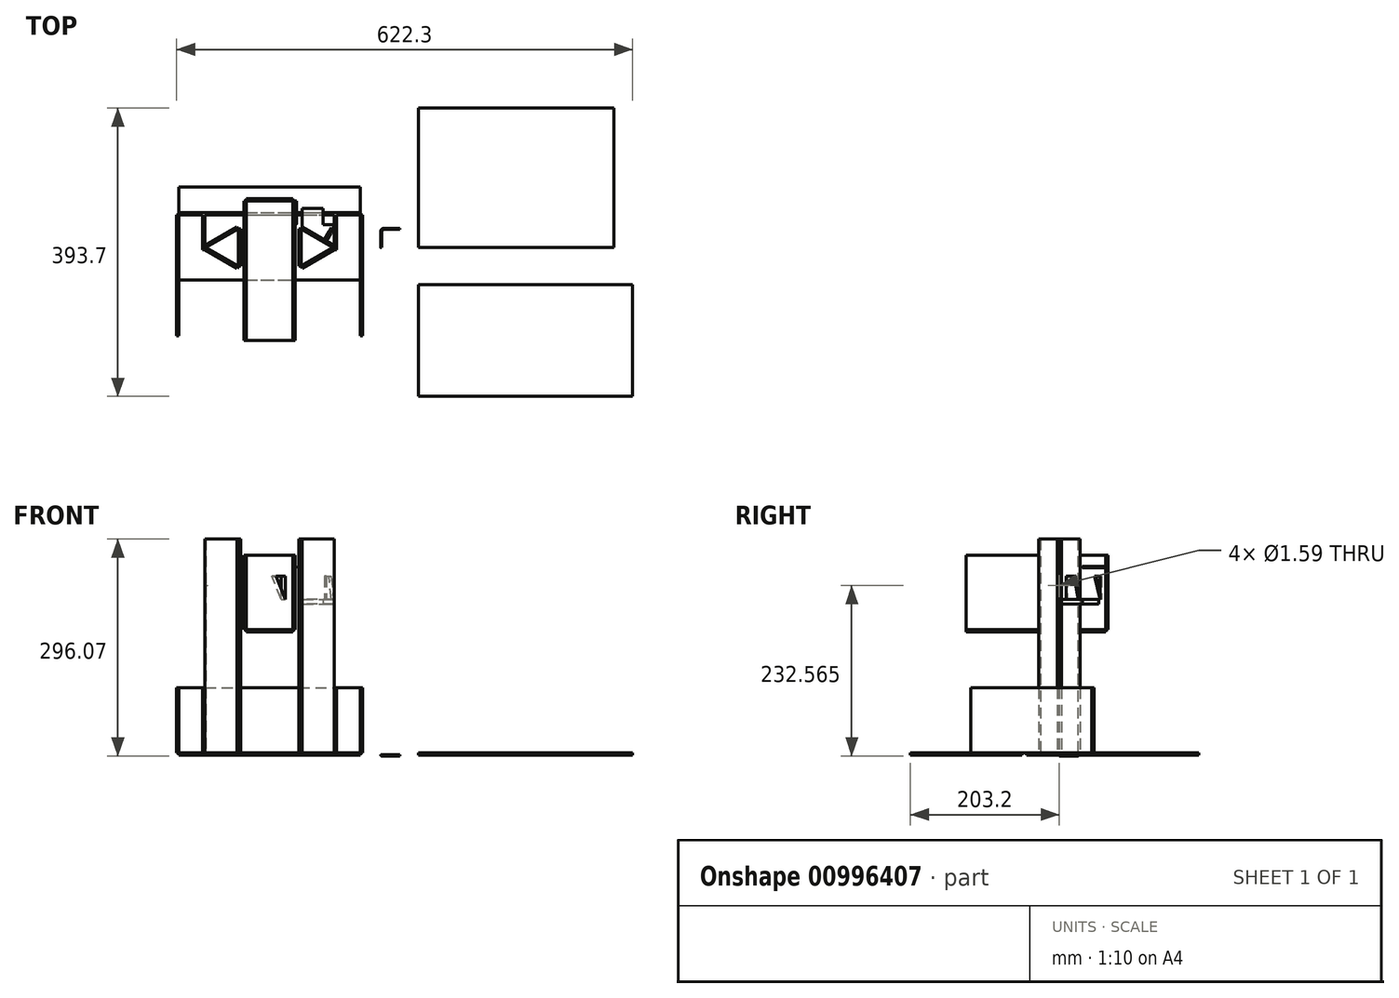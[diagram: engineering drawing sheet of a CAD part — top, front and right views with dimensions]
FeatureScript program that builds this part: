
annotation { "Feature Type Name" : "Feature", "Feature Type Description" : "" }
export const myFeature = defineFeature(function(context is Context, id is Id, definition is map)
    precondition{}
    {
        {
            var Q0;
            Q0=qCreatedBy(makeId("Top.planeOp"),FACE);
            var sketch = newSketch(context, id + "F0", { "sketchPlane" : qUnion([Q0])});
            skLineSegment(sketch, "E0.bottom", {"start": v(-123.83, -44.45) * mm, "end": v(123.83, -44.45) * mm});
            skLineSegment(sketch, "E0.top", {"start": v(-123.83, 44.45) * mm, "end": v(123.83, 44.45) * mm});
            skLineSegment(sketch, "E0.left", {"start": v(-123.83, -44.45) * mm, "end": v(-123.83, 44.45) * mm});
            skLineSegment(sketch, "E0.right", {"start": v(123.83, -44.45) * mm, "end": v(123.83, 44.45) * mm});
            skPoint(sketch, "E0.middle", {"position": v(0, 0) * mm});
            skSolve(sketch);
        }
        {
            var Q0;
            Q0 = qSketchRegion(id + "F0", true);
            extrude(context, id + "F1", {"entities" : qUnion([Q0]), "depth" : 3.17 * mm, "offsetDistance" : 25.4 * mm});
        }
        {
            var Q0;
            Q0=makeQuery(id+"F1.opExtrude","CAP_FACE",FACE,{"disambiguationData":[OSD([sQuery(id+"F0.wireOp",EDGE,"E0.bottom"),sQuery(id+"F0.wireOp",EDGE,"E0.top"),sQuery(id+"F0.wireOp",EDGE,"E0.left"),sQuery(id+"F0.wireOp",EDGE,"E0.right")])],"isStart":false});
            var sketch = newSketch(context, id + "F2", { "sketchPlane" : qUnion([Q0])});
            skLineSegment(sketch, "E1.bottom", {"start": v(-123.83, 44.45) * mm, "end": v(-127, 44.45) * mm});
            skLineSegment(sketch, "E1.top", {"start": v(-123.82, -120.65) * mm, "end": v(-127, -120.65) * mm});
            skLineSegment(sketch, "E1.left", {"start": v(-123.83, 44.45) * mm, "end": v(-123.82, -120.65) * mm});
            skLineSegment(sketch, "E1.right", {"start": v(-127, 44.45) * mm, "end": v(-127, -120.65) * mm});
            skSolve(sketch);
        }
        {
            var Q0;
            Q0 = qSketchRegion(id + "F2", true);
            extrude(context, id + "F3", {"entities" : qUnion([Q0]), "depth" : 88.9 * mm, "offsetDistance" : 25.4 * mm});
        }
        {
            var Q0;
            Q0=makeQuery(id+"F3.opExtrude","SWEPT_BODY",BODY,{"disambiguationData":[OSD([sQuery(id+"F2.wireOp",EDGE,"E1.bottom"),sQuery(id+"F2.wireOp",EDGE,"E1.top"),sQuery(id+"F2.wireOp",EDGE,"E1.left"),sQuery(id+"F2.wireOp",EDGE,"E1.right")])]});
            var Q1;
            Q1=qCreatedBy(makeId("Right.planeOp"),FACE);
            mirror(context, id + "F4", {"operationType" : NewBodyOperationType.ADD, "entities" : qUnion([Q0]), "mirrorPlane" : qUnion([Q1])});
        }
        {
            var Q0;
            Q0=makeQuery(id+"F1.opExtrude","CAP_FACE",FACE,{"disambiguationData":[OSD([sQuery(id+"F0.wireOp",EDGE,"E0.bottom"),sQuery(id+"F0.wireOp",EDGE,"E0.top"),sQuery(id+"F0.wireOp",EDGE,"E0.left"),sQuery(id+"F0.wireOp",EDGE,"E0.right")])],"isStart":false});
            var sketch = newSketch(context, id + "F5", { "sketchPlane" : qUnion([Q0])});
            skLineSegment(sketch, "E2.bottom", {"start": v(-123.83, 44.45) * mm, "end": v(123.83, 44.45) * mm});
            skLineSegment(sketch, "E2.top", {"start": v(-123.83, 47.62) * mm, "end": v(123.83, 47.62) * mm});
            skLineSegment(sketch, "E2.left", {"start": v(-123.83, 44.45) * mm, "end": v(-123.83, 47.62) * mm});
            skLineSegment(sketch, "E2.right", {"start": v(123.83, 44.45) * mm, "end": v(123.83, 47.62) * mm});
            skSolve(sketch);
        }
        {
            var Q0;
            Q0 = qSketchRegion(id + "F5", true);
            var Q1;
            Q1=makeQuery(id+"F3.opExtrude","CAP_FACE",FACE,{"disambiguationData":[OSD([sQuery(id+"F2.wireOp",EDGE,"E1.bottom"),sQuery(id+"F2.wireOp",EDGE,"E1.top"),sQuery(id+"F2.wireOp",EDGE,"E1.left"),sQuery(id+"F2.wireOp",EDGE,"E1.right")])],"isStart":false});
            extrude(context, id + "F6", {"entities" : qUnion([Q0]), "endBound" : BoundingType.UP_TO_SURFACE, "depth" : 25.4 * mm, "endBoundEntityFace" : qUnion([Q1]), "offsetDistance" : 25.4 * mm});
        }
        {
            var Q0;
            Q0=makeQuery(id+"F1.opExtrude","CAP_FACE",FACE,{"disambiguationData":[OSD([sQuery(id+"F0.wireOp",EDGE,"E0.bottom"),sQuery(id+"F0.wireOp",EDGE,"E0.top"),sQuery(id+"F0.wireOp",EDGE,"E0.left"),sQuery(id+"F0.wireOp",EDGE,"E0.right")])],"isStart":false});
            var sketch = newSketch(context, id + "F7", { "sketchPlane" : qUnion([Q0])});
            skLineSegment(sketch, "E3", {"start": v(0, 0) * mm, "end": v(39.69, 0) * mm, "construction": true});
            skLineSegment(sketch, "E4", {"start": v(0, 0) * mm, "end": v(-39.69, 0) * mm, "construction": true});
            skLineSegment(sketch, "E5", {"start": v(-39.69, 25.4) * mm, "end": v(-39.69, -25.4) * mm, "construction": true});
            skLineSegment(sketch, "E6.bottom", {"start": v(-39.69, 25.4) * mm, "end": v(-42.86, 25.4) * mm});
            skLineSegment(sketch, "E6.top", {"start": v(-39.69, -25.4) * mm, "end": v(-42.86, -25.4) * mm});
            skLineSegment(sketch, "E6.left", {"start": v(-39.69, 25.4) * mm, "end": v(-39.69, -25.4) * mm});
            skLineSegment(sketch, "E6.right", {"start": v(-42.86, 25.4) * mm, "end": v(-42.86, -25.4) * mm});
            skSolve(sketch);
        }
        {
            var Q0;
            Q0 = qSketchRegion(id + "F7", true);
            extrude(context, id + "F8", {"entities" : qUnion([Q0]), "depth" : 292.1 * mm, "offsetDistance" : 25.4 * mm});
        }
        {
            var Q0;
            Q0=makeQuery(id+"F1.opExtrude","CAP_FACE",FACE,{"disambiguationData":[OSD([sQuery(id+"F0.wireOp",EDGE,"E0.bottom"),sQuery(id+"F0.wireOp",EDGE,"E0.top"),sQuery(id+"F0.wireOp",EDGE,"E0.left"),sQuery(id+"F0.wireOp",EDGE,"E0.right")])],"isStart":false});
            var sketch = newSketch(context, id + "F9", { "sketchPlane" : qUnion([Q0])});
            skLineSegment(sketch, "E7", {"start": v(-42.86, 25.4) * mm, "end": v(-86.86, 0) * mm, "construction": true});
            skLineSegment(sketch, "E8", {"start": v(-86.86, 0) * mm, "end": v(-42.86, -25.4) * mm, "construction": true});
            skLineSegment(sketch, "E9.bottom", {"start": v(-88.44, 2.75) * mm, "end": v(-44.45, 28.15) * mm});
            skLineSegment(sketch, "E9.top", {"start": v(-86.86, 0) * mm, "end": v(-42.86, 25.4) * mm});
            skLineSegment(sketch, "E9.left", {"start": v(-88.44, 2.75) * mm, "end": v(-86.86, 0) * mm});
            skLineSegment(sketch, "E9.right", {"start": v(-44.45, 28.15) * mm, "end": v(-42.86, 25.4) * mm});
            skLineSegment(sketch, "E10.bottom", {"start": v(-86.86, 0) * mm, "end": v(-42.86, -25.4) * mm});
            skLineSegment(sketch, "E10.top", {"start": v(-88.44, -2.75) * mm, "end": v(-44.45, -28.15) * mm});
            skLineSegment(sketch, "E10.left", {"start": v(-86.86, 0) * mm, "end": v(-88.44, -2.75) * mm});
            skLineSegment(sketch, "E10.right", {"start": v(-42.86, -25.4) * mm, "end": v(-44.45, -28.15) * mm});
            skSolve(sketch);
        }
        {
            var Q0;
            Q0=makeQuery(id+"F9.imprint","IMPRINT",FACE,{"disambiguationData":[TD([[makeQuery(id+"F9.imprint","IMPRINT",EDGE,{"derivedFrom":sQuery(id+"F9.wireOp",EDGE,"E10.bottom")}),-1.0]])]});
            var Q1;
            Q1=makeQuery(id+"F9.imprint","IMPRINT",FACE,{"disambiguationData":[TD([[makeQuery(id+"F9.imprint","IMPRINT",EDGE,{"derivedFrom":sQuery(id+"F9.wireOp",EDGE,"E9.bottom")}),-1.0]])]});
            var Q2;
            Q2=makeQuery(id+"F8.opExtrude","CAP_FACE",FACE,{"disambiguationData":[OSD([sQuery(id+"F7.wireOp",EDGE,"E6.bottom"),sQuery(id+"F7.wireOp",EDGE,"E6.top"),sQuery(id+"F7.wireOp",EDGE,"E6.left"),sQuery(id+"F7.wireOp",EDGE,"E6.right")])],"isStart":false});
            extrude(context, id + "F10", {"entities" : qUnion([Q0, Q1]), "endBound" : BoundingType.UP_TO_SURFACE, "depth" : 25.4 * mm, "endBoundEntityFace" : qUnion([Q2]), "offsetDistance" : 25.4 * mm});
        }
        {
            var Q0;
            Q0=makeQuery(id+"F10.opExtrude","SWEPT_BODY",BODY,{"disambiguationData":[OSD([sQuery(id+"F9.wireOp",EDGE,"E10.bottom"),sQuery(id+"F9.wireOp",EDGE,"E10.top"),sQuery(id+"F9.wireOp",EDGE,"E10.left"),sQuery(id+"F9.wireOp",EDGE,"E10.right")])]});
            var Q1;
            Q1=makeQuery(id+"F10.opExtrude","SWEPT_BODY",BODY,{"disambiguationData":[OSD([sQuery(id+"F9.wireOp",EDGE,"E9.bottom"),sQuery(id+"F9.wireOp",EDGE,"E9.top"),sQuery(id+"F9.wireOp",EDGE,"E9.left"),sQuery(id+"F9.wireOp",EDGE,"E9.right")])]});
            var Q2;
            Q2=makeQuery(id+"F8.opExtrude","SWEPT_BODY",BODY,{"disambiguationData":[OSD([sQuery(id+"F7.wireOp",EDGE,"E6.bottom"),sQuery(id+"F7.wireOp",EDGE,"E6.top"),sQuery(id+"F7.wireOp",EDGE,"E6.left"),sQuery(id+"F7.wireOp",EDGE,"E6.right")])]});
            var Q3;
            Q3=qCreatedBy(makeId("Right.planeOp"),FACE);
            mirror(context, id + "F11", {"entities" : qUnion([Q0, Q1, Q2]), "mirrorPlane" : qUnion([Q3])});
        }
        {
            var Q0;
            Q0=makeQuery(id+"F1.opExtrude","CAP_FACE",FACE,{"disambiguationData":[OSD([sQuery(id+"F0.wireOp",EDGE,"E0.bottom"),sQuery(id+"F0.wireOp",EDGE,"E0.top"),sQuery(id+"F0.wireOp",EDGE,"E0.left"),sQuery(id+"F0.wireOp",EDGE,"E0.right")])],"isStart":false});
            var sketch = newSketch(context, id + "F12", { "sketchPlane" : qUnion([Q0])});
            skLineSegment(sketch, "E11.bottom", {"start": v(-91.62, 44.45) * mm, "end": v(-88.44, 44.45) * mm});
            skLineSegment(sketch, "E11.top", {"start": v(-91.62, -2.75) * mm, "end": v(-88.44, -2.75) * mm});
            skLineSegment(sketch, "E11.left", {"start": v(-91.62, 44.45) * mm, "end": v(-91.62, -2.75) * mm});
            skLineSegment(sketch, "E11.right", {"start": v(-88.44, 44.45) * mm, "end": v(-88.44, -2.75) * mm});
            skSolve(sketch);
        }
        {
            var Q0;
            Q0 = qSketchRegion(id + "F12", true);
            var Q1;
            Q1=makeQuery(id+"F6.opExtrude","CAP_FACE",FACE,{"disambiguationData":[OSD([sQuery(id+"F5.wireOp",EDGE,"E2.bottom"),sQuery(id+"F5.wireOp",EDGE,"E2.top"),sQuery(id+"F5.wireOp",EDGE,"E2.left"),sQuery(id+"F5.wireOp",EDGE,"E2.right")])],"isStart":false});
            extrude(context, id + "F13", {"entities" : qUnion([Q0]), "endBound" : BoundingType.UP_TO_SURFACE, "depth" : 101.6 * mm, "endBoundEntityFace" : qUnion([Q1]), "offsetDistance" : 25.4 * mm});
        }
        {
            var Q0;
            Q0=makeQuery(id+"F1.opExtrude","CAP_FACE",FACE,{"disambiguationData":[OSD([sQuery(id+"F0.wireOp",EDGE,"E0.bottom"),sQuery(id+"F0.wireOp",EDGE,"E0.top"),sQuery(id+"F0.wireOp",EDGE,"E0.left"),sQuery(id+"F0.wireOp",EDGE,"E0.right")])],"isStart":false});
            var sketch = newSketch(context, id + "F14", { "sketchPlane" : qUnion([Q0])});
            skLineSegment(sketch, "E12.bottom", {"start": v(88.44, -2.75) * mm, "end": v(91.62, -2.75) * mm});
            skLineSegment(sketch, "E12.top", {"start": v(88.44, 44.45) * mm, "end": v(91.62, 44.45) * mm});
            skLineSegment(sketch, "E12.left", {"start": v(88.44, 44.45) * mm, "end": v(88.44, -2.75) * mm});
            skLineSegment(sketch, "E12.right", {"start": v(91.62, 44.45) * mm, "end": v(91.62, -2.75) * mm});
            skSolve(sketch);
        }
        {
            var Q0;
            Q0 = qSketchRegion(id + "F14", true);
            var Q1;
            Q1=makeQuery(id+"F4.opPattern","COPY",FACE,{"derivedFrom":makeQuery(id+"F3.opExtrude","CAP_FACE",FACE,{"disambiguationData":[OSD([sQuery(id+"F2.wireOp",EDGE,"E1.bottom"),sQuery(id+"F2.wireOp",EDGE,"E1.top"),sQuery(id+"F2.wireOp",EDGE,"E1.left"),sQuery(id+"F2.wireOp",EDGE,"E1.right")])],"isStart":false}),"instanceName":"1"});
            extrude(context, id + "F15", {"entities" : qUnion([Q0]), "endBound" : BoundingType.UP_TO_SURFACE, "depth" : 25.4 * mm, "endBoundEntityFace" : qUnion([Q1]), "offsetDistance" : 25.4 * mm});
        }
        {
            var Q0;
            Q0=qCreatedBy(makeId("Right.planeOp"),FACE);
            var sketch = newSketch(context, id + "F16", { "sketchPlane" : qUnion([Q0])});
            skCircle(sketch, "E13", {"center": v(0, 231.78) * mm, "radius": 0.8 * mm});
            skLineSegment(sketch, "E14.0", {"start": v(25.4, 295.28) * mm, "end": v(-25.4, 295.28) * mm, "construction": true});
            skLineSegment(sketch, "E15", {"start": v(0, 295.28) * mm, "end": v(0, 231.78) * mm, "construction": true});
            skSolve(sketch);
        }
        {
            var Q0;
            Q0 = qSketchRegion(id + "F16", true);
            extrude(context, id + "F17", {"entities" : qUnion([Q0]), "operationType" : NewBodyOperationType.REMOVE, "endBound" : BoundingType.SYMMETRIC, "oppositeDirection" : true, "depth" : 101.6 * mm, "offsetDistance" : 25.4 * mm});
        }
        {
            var Q0;
            Q0=makeQuery(id+"F8.opExtrude","CAP_FACE",FACE,{"disambiguationData":[OSD([sQuery(id+"F7.wireOp",EDGE,"E6.bottom"),sQuery(id+"F7.wireOp",EDGE,"E6.top"),sQuery(id+"F7.wireOp",EDGE,"E6.left"),sQuery(id+"F7.wireOp",EDGE,"E6.right")])],"isStart":false});
            cPlane(context, id + "F18", {"entities" : qUnion([Q0]), "cplaneType" : CPlaneType.OFFSET, "offset" : 127 * mm, "oppositeDirection" : true, "width" : 152.4 * mm, "height" : 152.4 * mm});
        }
        {
            var Q0;
            Q0=qCreatedBy(id+"F18.planeOp",FACE);
            var sketch = newSketch(context, id + "F19", { "sketchPlane" : qUnion([Q0])});
            skLineSegment(sketch, "E16.bottom", {"start": v(31.75, 63.5) * mm, "end": v(-31.75, 63.5) * mm});
            skLineSegment(sketch, "E16.top", {"start": v(31.75, -127) * mm, "end": v(-31.75, -127) * mm});
            skLineSegment(sketch, "E16.left", {"start": v(31.75, 63.5) * mm, "end": v(31.75, -127) * mm});
            skLineSegment(sketch, "E16.right", {"start": v(-31.75, 63.5) * mm, "end": v(-31.75, -127) * mm});
            skPoint(sketch, "E16.middle", {"position": v(0, -31.75) * mm});
            skSolve(sketch);
        }
        {
            var Q0;
            Q0 = qSketchRegion(id + "F19", true);
            extrude(context, id + "F20", {"entities" : qUnion([Q0]), "depth" : 3.17 * mm, "offsetDistance" : 25.4 * mm});
        }
        {
            var Q0;
            Q0=makeQuery(id+"F20.opExtrude","CAP_FACE",FACE,{"disambiguationData":[OSD([sQuery(id+"F19.wireOp",EDGE,"E16.bottom"),sQuery(id+"F19.wireOp",EDGE,"E16.top"),sQuery(id+"F19.wireOp",EDGE,"E16.left"),sQuery(id+"F19.wireOp",EDGE,"E16.right")])],"isStart":false});
            var sketch = newSketch(context, id + "F21", { "sketchPlane" : qUnion([Q0])});
            skLineSegment(sketch, "E17.bottom", {"start": v(-31.75, -127) * mm, "end": v(-34.92, -127) * mm});
            skLineSegment(sketch, "E17.top", {"start": v(-31.75, 63.5) * mm, "end": v(-34.92, 63.5) * mm});
            skLineSegment(sketch, "E17.left", {"start": v(-31.75, -127) * mm, "end": v(-31.75, 63.5) * mm});
            skLineSegment(sketch, "E17.right", {"start": v(-34.92, -127) * mm, "end": v(-34.92, 63.5) * mm});
            skLineSegment(sketch, "E18.bottom", {"start": v(31.75, -127) * mm, "end": v(34.92, -127) * mm});
            skLineSegment(sketch, "E18.top", {"start": v(31.75, 63.5) * mm, "end": v(34.92, 63.5) * mm});
            skLineSegment(sketch, "E18.left", {"start": v(31.75, -127) * mm, "end": v(31.75, 63.5) * mm});
            skLineSegment(sketch, "E18.right", {"start": v(34.92, -127) * mm, "end": v(34.92, 63.5) * mm});
            skSolve(sketch);
        }
        {
            var Q0;
            Q0 = qSketchRegion(id + "F21", true);
            extrude(context, id + "F22", {"entities" : qUnion([Q0]), "depth" : 101.6 * mm, "offsetDistance" : 25.4 * mm});
        }
        {
            var Q0;
            Q0=makeQuery(id+"F22.opExtrude","SWEPT_FACE",FACE,{"disambiguationData":[OSD([sQuery(id+"F21.wireOp",EDGE,"E18.top")])]});
            var sketch = newSketch(context, id + "F23", { "sketchPlane" : qUnion([Q0])});
            skLineSegment(sketch, "E19.0", {"start": v(-31.75, 273.05) * mm, "end": v(-31.75, 171.45) * mm});
            skLineSegment(sketch, "E20.0", {"start": v(31.75, 273.05) * mm, "end": v(31.75, 171.45) * mm});
            skLineSegment(sketch, "E21.0", {"start": v(-31.75, 171.45) * mm, "end": v(31.75, 171.45) * mm});
            skLineSegment(sketch, "E22", {"start": v(-31.75, 273.05) * mm, "end": v(31.75, 273.05) * mm});
            skSolve(sketch);
        }
        {
            var Q0;
            Q0 = qSketchRegion(id + "F23", true);
            extrude(context, id + "F24", {"entities" : qUnion([Q0]), "depth" : 3.17 * mm, "offsetDistance" : 25.4 * mm});
        }
        {
            var Q0;
            Q0=makeQuery(id+"F22.opExtrude","SWEPT_FACE",FACE,{"disambiguationData":[OSD([sQuery(id+"F21.wireOp",EDGE,"E18.right")])]});
            var sketch = newSketch(context, id + "F25", { "sketchPlane" : qUnion([Q0])});
            skCircle(sketch, "E23.0", {"center": v(0, 231.78) * mm, "radius": 0.8 * mm});
            skSolve(sketch);
        }
        {
            var Q0;
            Q0 = qSketchRegion(id + "F25", true);
            extrude(context, id + "F26", {"entities" : qUnion([Q0]), "operationType" : NewBodyOperationType.REMOVE, "endBound" : BoundingType.THROUGH_ALL, "oppositeDirection" : true, "depth" : 25.4 * mm, "offsetDistance" : 25.4 * mm});
        }
        {
            var Q0;
            Q0=qCreatedBy(makeId("Top.planeOp"),FACE);
            var sketch = newSketch(context, id + "F27", { "sketchPlane" : qUnion([Q0])});
            skLineSegment(sketch, "E24", {"start": v(152.4, 0) * mm, "end": v(152.4, 22.23) * mm});
            skLineSegment(sketch, "E25", {"start": v(155.58, 25.4) * mm, "end": v(177.8, 25.4) * mm});
            skPoint(sketch, "E26.visualSharp", {"position": v(152.4, 25.4) * mm});
            skArc(sketch, "E26.filletArc", {"start": v(155.58, 25.4) * mm, "mid": v(153.33, 24.47) * mm, "end": v(152.4, 22.23) * mm});
            skSolve(sketch);
        }
        {
            var Q0;
            Q0=qCreatedBy(makeId("Front.planeOp"),FACE);
            var sketch = newSketch(context, id + "F28", { "sketchPlane" : qUnion([Q0])});
            skCircle(sketch, "E27", {"center": v(152.4, 0) * mm, "radius": 0.8 * mm});
            skSolve(sketch);
        }
        {
            var Q0;
            Q0=makeQuery(id+"F28.imprint","IMPRINT",FACE,{"disambiguationData":[TD([[makeQuery(id+"F28.imprint","IMPRINT",EDGE,{"derivedFrom":sQuery(id+"F28.wireOp",EDGE,"E27")}),1.0]])]});
            var Q1;
            Q1=sQuery(id+"F27.wireOp",EDGE,"E24");
            var Q2;
            Q2=sQuery(id+"F27.wireOp",EDGE,"E26.filletArc");
            var Q3;
            Q3=sQuery(id+"F27.wireOp",EDGE,"E25");
            sweep(context, id + "F29", {"profiles" : qUnion([Q0]), "path" : qUnion([Q1, Q2, Q3])});
        }
        {
            var Q0;
            Q0=makeQuery(id+"F22.opExtrude","SWEPT_FACE",FACE,{"disambiguationData":[OSD([sQuery(id+"F21.wireOp",EDGE,"E18.top")])]});
            var sketch = newSketch(context, id + "F30", { "sketchPlane" : qUnion([Q0])});
            skCircle(sketch, "E28", {"center": v(-35.72, 257.18) * mm, "radius": 0.8 * mm});
            skSolve(sketch);
        }
        {
            var Q0;
            Q0 = qSketchRegion(id + "F30", true);
            extrude(context, id + "F31", {"entities" : qUnion([Q0]), "operationType" : NewBodyOperationType.ADD, "oppositeDirection" : true, "depth" : 31.75 * mm, "offsetDistance" : 25.4 * mm});
        }
        {
            var Q0;
            Q0=qCreatedBy(id+"F18.planeOp",FACE);
            cPlane(context, id + "F32", {"entities" : qUnion([Q0]), "cplaneType" : CPlaneType.OFFSET, "offset" : 38.1 * mm, "width" : 152.4 * mm, "height" : 152.4 * mm});
        }
        {
            var Q0;
            Q0=qCreatedBy(id+"F32.planeOp",FACE);
            var sketch = newSketch(context, id + "F33", { "sketchPlane" : qUnion([Q0])});
            skLineSegment(sketch, "E29.0", {"start": v(88.44, 2.75) * mm, "end": v(44.45, 28.15) * mm});
            skLineSegment(sketch, "E30", {"start": v(44.45, 28.15) * mm, "end": v(44.45, 53.55) * mm});
            skLineSegment(sketch, "E31", {"start": v(44.45, 53.55) * mm, "end": v(73.02, 53.55) * mm});
            skLineSegment(sketch, "E32", {"start": v(73.02, 53.55) * mm, "end": v(73.02, 31.32) * mm});
            skLineSegment(sketch, "E33", {"start": v(73.02, 31.32) * mm, "end": v(88.44, 31.32) * mm});
            skLineSegment(sketch, "E34", {"start": v(88.44, 2.75) * mm, "end": v(88.44, 31.32) * mm});
            skSolve(sketch);
        }
        {
            var Q0;
            Q0 = qSketchRegion(id + "F33", true);
            extrude(context, id + "F34", {"entities" : qUnion([Q0]), "depth" : 6.35 * mm, "offsetDistance" : 25.4 * mm});
        }
        {
            var Q0;
            Q0=makeQuery(id+"F34.opExtrude","CAP_FACE",FACE,{"disambiguationData":[OSD([sQuery(id+"F33.wireOp",EDGE,"E29.0"),sQuery(id+"F33.wireOp",EDGE,"E30"),sQuery(id+"F33.wireOp",EDGE,"E31"),sQuery(id+"F33.wireOp",EDGE,"E32"),sQuery(id+"F33.wireOp",EDGE,"E33"),sQuery(id+"F33.wireOp",EDGE,"E34")])],"isStart":false});
            var sketch = newSketch(context, id + "F35", { "sketchPlane" : qUnion([Q0])});
            skLineSegment(sketch, "E35", {"start": v(76.07, 9.9) * mm, "end": v(88.44, 31.32) * mm, "construction": true});
            skLineSegment(sketch, "E36.bottom", {"start": v(77.45, 9.1) * mm, "end": v(74.7, 10.69) * mm});
            skLineSegment(sketch, "E36.top", {"start": v(86.97, 25.6) * mm, "end": v(84.22, 27.18) * mm});
            skLineSegment(sketch, "E36.left", {"start": v(77.45, 9.1) * mm, "end": v(86.97, 25.6) * mm});
            skLineSegment(sketch, "E36.right", {"start": v(74.7, 10.69) * mm, "end": v(84.22, 27.18) * mm});
            skSolve(sketch);
        }
        {
            var Q0;
            Q0 = qSketchRegion(id + "F35", true);
            extrude(context, id + "F36", {"entities" : qUnion([Q0]), "depth" : 31.75 * mm, "offsetDistance" : 25.4 * mm});
        }
        {
            var Q0;
            Q0=makeQuery(id+"F36.opExtrude","SWEPT_FACE",FACE,{"disambiguationData":[OSD([sQuery(id+"F35.wireOp",EDGE,"E36.left")])]});
            var sketch = newSketch(context, id + "F37", { "sketchPlane" : qUnion([Q0])});
            skLineSegment(sketch, "E37.0", {"start": v(59.3, 244.47) * mm, "end": v(65.65, 244.47) * mm});
            skLineSegment(sketch, "E38.0", {"start": v(65.65, 244.47) * mm, "end": v(65.65, 212.72) * mm});
            skLineSegment(sketch, "E39", {"start": v(59.3, 244.47) * mm, "end": v(65.65, 212.72) * mm});
            skPoint(sketch, "E40.orphan", {"position": v(46.6, 244.47) * mm});
            skSolve(sketch);
        }
        {
            var Q0;
            Q0 = qSketchRegion(id + "F37", true);
            extrude(context, id + "F38", {"entities" : qUnion([Q0]), "operationType" : NewBodyOperationType.REMOVE, "endBound" : BoundingType.THROUGH_ALL, "oppositeDirection" : true, "depth" : 25.4 * mm, "offsetDistance" : 25.4 * mm});
        }
        {
            var Q0;
            Q0=qCreatedBy(makeId("Top.planeOp"),FACE);
            var sketch = newSketch(context, id + "F39", { "sketchPlane" : qUnion([Q0])});
            skLineSegment(sketch, "E41.bottom", {"start": v(203.2, 190.5) * mm, "end": v(469.9, 190.5) * mm});
            skLineSegment(sketch, "E41.top", {"start": v(203.2, 0) * mm, "end": v(469.9, 0) * mm});
            skLineSegment(sketch, "E41.left", {"start": v(203.2, 190.5) * mm, "end": v(203.2, 0) * mm});
            skLineSegment(sketch, "E41.right", {"start": v(469.9, 190.5) * mm, "end": v(469.9, 0) * mm});
            skLineSegment(sketch, "E42", {"start": v(304.8, 190.5) * mm, "end": v(304.8, 0) * mm, "construction": true});
            skLineSegment(sketch, "E43", {"start": v(368.3, 190.5) * mm, "end": v(368.3, 0) * mm, "construction": true});
            skSolve(sketch);
        }
        {
            var Q0;
            Q0 = qSketchRegion(id + "F39", true);
            extrude(context, id + "F40", {"entities" : qUnion([Q0]), "depth" : 3.17 * mm, "offsetDistance" : 25.4 * mm});
        }
        {
            var Q0;
            Q0=qCreatedBy(makeId("Top.planeOp"),FACE);
            var sketch = newSketch(context, id + "F41", { "sketchPlane" : qUnion([Q0])});
            skLineSegment(sketch, "E44.bottom", {"start": v(203.2, -50.8) * mm, "end": v(495.3, -50.8) * mm});
            skLineSegment(sketch, "E44.top", {"start": v(203.2, -203.2) * mm, "end": v(495.3, -203.2) * mm});
            skLineSegment(sketch, "E44.left", {"start": v(203.2, -50.8) * mm, "end": v(203.2, -203.2) * mm});
            skLineSegment(sketch, "E44.right", {"start": v(495.3, -50.8) * mm, "end": v(495.3, -203.2) * mm});
            skSolve(sketch);
        }
        {
            var Q0;
            Q0 = qSketchRegion(id + "F41", true);
            extrude(context, id + "F42", {"entities" : qUnion([Q0]), "depth" : 3.17 * mm, "offsetDistance" : 25.4 * mm});
        }
        {
            var Q0;
            Q0=makeQuery(id+"F1.opExtrude","SWEPT_FACE",FACE,{"disambiguationData":[OSD([sQuery(id+"F0.wireOp",EDGE,"E0.top")])]});
            var sketch = newSketch(context, id + "F43", { "sketchPlane" : qUnion([Q0])});
            skLineSegment(sketch, "E45.0.0", {"start": v(-123.83, 0) * mm, "end": v(123.83, 0) * mm});
            skLineSegment(sketch, "E45.0.1", {"start": v(123.83, 0) * mm, "end": v(123.83, 3.18) * mm});
            skLineSegment(sketch, "E45.0.2", {"start": v(123.83, 3.18) * mm, "end": v(-123.83, 3.18) * mm});
            skLineSegment(sketch, "E45.0.3", {"start": v(-123.83, 3.18) * mm, "end": v(-123.83, 0) * mm});
            skSolve(sketch);
        }
        {
            var Q0;
            Q0 = qSketchRegion(id + "F43", true);
            extrude(context, id + "F44", {"entities" : qUnion([Q0]), "operationType" : NewBodyOperationType.ADD, "depth" : 38.1 * mm, "offsetDistance" : 25.4 * mm});
        }
    });
